# Revit family: Partition-8_Panels_High-Skyfold_Classic_Compact-14-1_to_16-1_FC_4295_to_4900
name_source: partatom
category: Generic Models
units: mm (PartAtom-declared; Revit-internal decimal feet)

## family parameters
Always vertical = Yes
Can host rebar = No
Cut with Voids When Loaded = No
Host = Ceiling
Maintain Annotation Orientation = No
Part Type = Normal
Room Calculation Point = No
Round Connector Dimension = Use Diameter
Shared = No

## types (6) — shared parameters
Default Elevation = 0' - 0"
Distance From Acoustic Barrier = 0' - 2"
Model = Compact Drive System
Pocket Depth"D" = 2' - 1 1/2"
URL = http://www.skyfold.com
Wall Thickness = 0' - 11 3/4"

## per-type parameters (varying)
| type | Acoustic Barrier"C" | Beam Height"B" | Description | Finished Ceiling"A" | Manufacturer | Panel Height"F" | Pocket Width"E" | Total Panel Height |
| 15'- 0" | 17' - 1 1/2" | 18' - 1 1/4" | Custom Powerlift Partitions | 15' - 0" | Skyfold | 2' - 0 7/8" | 4' - 11 1/2" | 16' - 10 1/2" |
| 16' - 1" | 18' - 2 1/2" | 19' - 2 1/4" | Custom Powerlift Partitions | 16' - 1" | Skyfold | 2' - 2 1/2" | 5' - 2 3/4" | 17' - 11 1/2" |
| 14' - 1" | 16' - 2 1/2" | 17' - 2 1/4" | Custom Powerlift Partitions
Custom Powerlift Partitions | 14' - 1" | Skyfold | 1' - 11 1/2" | 4' - 8 3/4" | 15' - 11 1/2" |
| 14' - 6" | 16' - 7 1/2" | 17' - 7 1/4" | Custom Powerlift Partitions | 14' - 6" | Skyfold | 2' - 0 1/8" | 4' - 10" | 16' - 4 1/2" |
| 16' - 0" | 18' - 1 1/2" | 19' - 1 1/4" | Custom Powerlift Partitions | 16' - 0" | Skyfold
Skyfold | 2' - 2 3/8" | 5' - 2 1/2" | 17' - 10 1/2" |
| 15' - 6" | 17' - 7 1/2" | 18' - 7 1/4" | Custom Powerlift Partitions
Custom Powerlift Partitions | 15' - 6" | Skyfold | 2' - 1 5/8" | 5' - 1" | 17' - 4 1/2" |

## geometry (parser evidence)
native form markers: Sweep x24
no freeform markers — native parametric forms only
